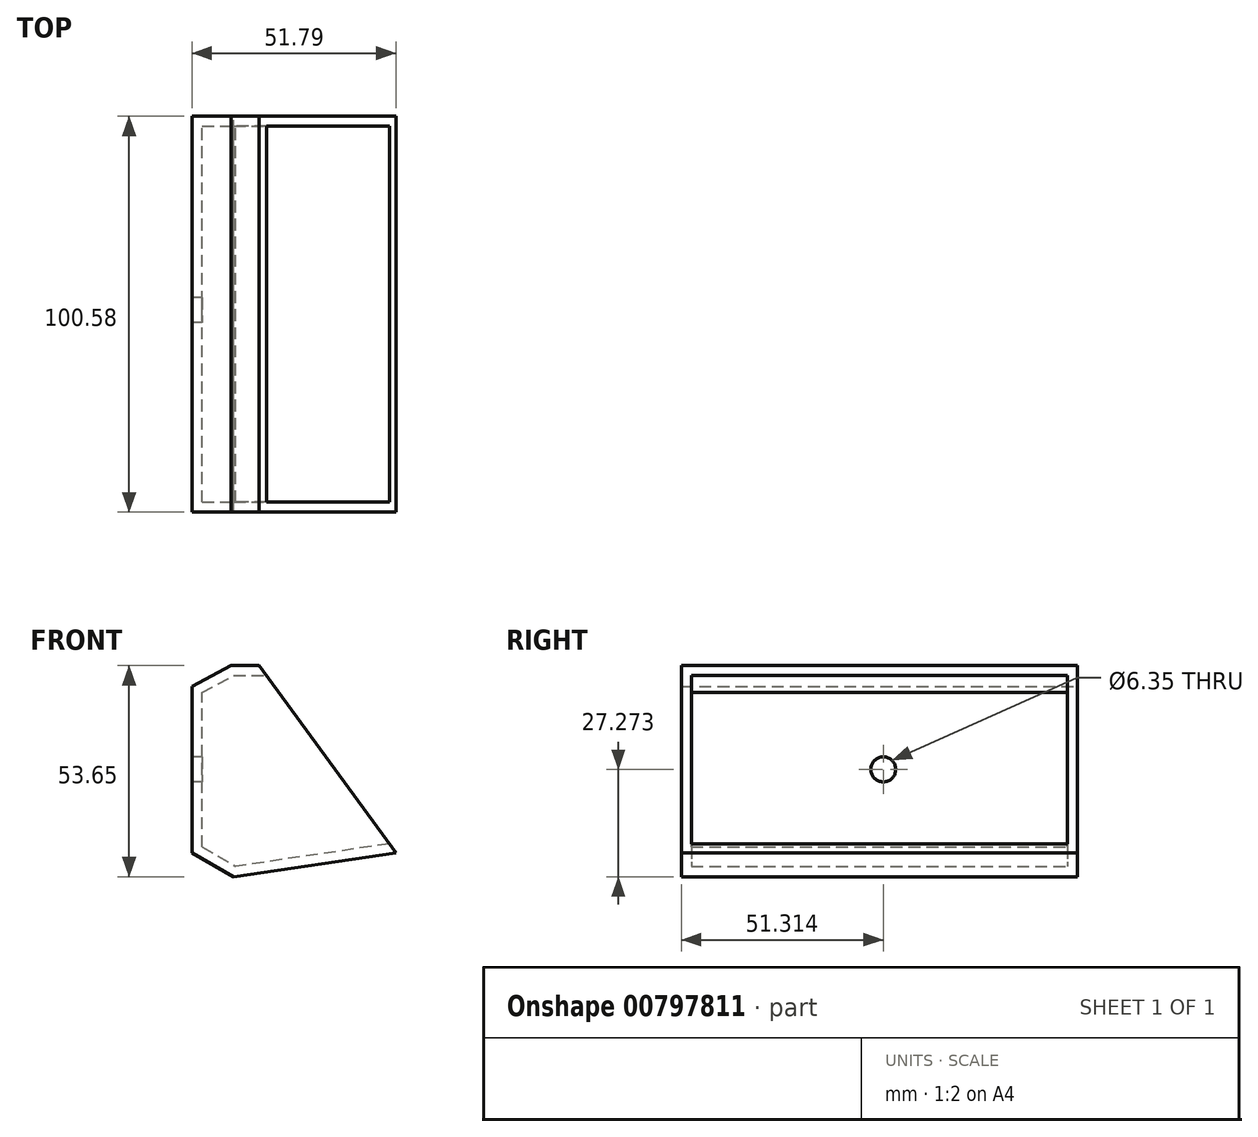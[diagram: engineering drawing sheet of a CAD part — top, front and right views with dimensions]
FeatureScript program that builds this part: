
annotation { "Feature Type Name" : "Feature", "Feature Type Description" : "" }
export const myFeature = defineFeature(function(context is Context, id is Id, definition is map)
    precondition{}
    {
        {
            var Q0;
            Q0=qCreatedBy(makeId("Front.planeOp"),FACE);
            var sketch = newSketch(context, id + "F0", { "sketchPlane" : qUnion([Q0])});
            skLineSegment(sketch, "E0", {"start": v(-45.74, 0) * mm, "end": v(-45.74, 42.33) * mm});
            skLineSegment(sketch, "E1", {"start": v(-45.74, 0) * mm, "end": v(-35.2, -6.05) * mm});
            skLineSegment(sketch, "E2", {"start": v(-45.74, 42.33) * mm, "end": v(-35.82, 47.6) * mm});
            skLineSegment(sketch, "E3", {"start": v(-35.82, 47.6) * mm, "end": v(-28.69, 47.6) * mm});
            skLineSegment(sketch, "E4", {"start": v(-28.69, 47.6) * mm, "end": v(6.05, 0) * mm});
            skLineSegment(sketch, "E5", {"start": v(6.05, 0) * mm, "end": v(-35.2, -6.05) * mm});
            skSolve(sketch);
        }
        {
            var Q0;
            Q0=makeQuery(id+"F0.imprint","IMPRINT",FACE,{"disambiguationData":[TD([[makeQuery(id+"F0.imprint","IMPRINT",EDGE,{"derivedFrom":sQuery(id+"F0.wireOp",EDGE,"E0")}),-1.0]])]});
            extrude(context, id + "F1", {"entities" : qUnion([Q0]), "depth" : 25.4 * mm, "offsetDistance" : 25.4 * mm});
        }
        {
            var Q0;
            Q0=makeQuery(id+"F1.opExtrude","CAP_FACE",FACE,{"disambiguationData":[OSD([sQuery(id+"F0.wireOp",EDGE,"E0"),sQuery(id+"F0.wireOp",EDGE,"E1"),sQuery(id+"F0.wireOp",EDGE,"E2"),sQuery(id+"F0.wireOp",EDGE,"E3"),sQuery(id+"F0.wireOp",EDGE,"E4"),sQuery(id+"F0.wireOp",EDGE,"E5")])],"isStart":true});
            extrude(context, id + "F2", {"entities" : qUnion([Q0]), "operationType" : NewBodyOperationType.ADD, "depth" : 75.18 * mm, "offsetDistance" : 25.4 * mm});
        }
        {
            var Q0;
            {var subQ0=sQuery(id+"F0.wireOp",EDGE,"E4");Q0=makeQuery(id+"F2.boolean.opBoolean","MERGE",FACE,{"derivedFrom":[makeQuery(id+"F1.opExtrude","SWEPT_FACE",FACE,{"disambiguationData":[OSD([subQ0])]}),makeQuery(id+"F2.opExtrude","SWEPT_FACE",FACE,{"disambiguationData":[OSD([subQ0])]})]});}
            shell(context, id + "F3", {"entities" : qUnion([Q0]), "thickness" : 2.54 * mm});
        }
        {
            var Q0;
            {var subQ0=sQuery(id+"F0.wireOp",EDGE,"E0");Q0=makeQuery(id+"F2.boolean.opBoolean","MERGE",FACE,{"derivedFrom":[makeQuery(id+"F1.opExtrude","SWEPT_FACE",FACE,{"disambiguationData":[OSD([subQ0])]}),makeQuery(id+"F2.opExtrude","SWEPT_FACE",FACE,{"disambiguationData":[OSD([subQ0])]})]});}
            var sketch = newSketch(context, id + "F4", { "sketchPlane" : qUnion([Q0])});
            skSolve(sketch);
        }
        {
            var Q0;
            {var subQ0=sQuery(id+"F0.wireOp",EDGE,"E0");Q0=makeQuery(id+"F4.imprint","IMPRINT",FACE,{"disambiguationData":[TD([[makeQuery(id+"F4.imprint","IMPRINT",EDGE,{"derivedFrom":makeQuery(id+"F1.opExtrude","CAP_EDGE",EDGE,{"disambiguationData":[OSD([subQ0])],"isStart":false})}),1.0]])]});}
            var sketch = newSketch(context, id + "F5", { "sketchPlane" : qUnion([Q0])});
            skCircle(sketch, "E6", {"center": v(-25.91, 21.22) * mm, "radius": 1.99 * mm});
            skSolve(sketch);
        }
        {
            var Q0;
            Q0=sQuery(id+"F5.wireOp",VERTEX,"E6.center");
            var Q1;
            Q1=makeQuery(id+"F1.opExtrude","SWEPT_BODY",BODY,{"disambiguationData":[OSD([sQuery(id+"F0.wireOp",EDGE,"E0"),sQuery(id+"F0.wireOp",EDGE,"E1"),sQuery(id+"F0.wireOp",EDGE,"E2"),sQuery(id+"F0.wireOp",EDGE,"E3"),sQuery(id+"F0.wireOp",EDGE,"E4"),sQuery(id+"F0.wireOp",EDGE,"E5")])]});
            hole(context, id + "F6", {"style" : HoleStyle.SIMPLE, "endStyle" : HoleEndStyle.THROUGH, "holeDiameter" : 6.35 * mm, "majorDiameter" : 6.35 * mm, "isTappedThrough" : true, "tappedDepth" : 12.7 * mm, "tapClearance" : 3, "locations" : qUnion([Q0]), "scope" : qUnion([Q1])});
        }
    });
